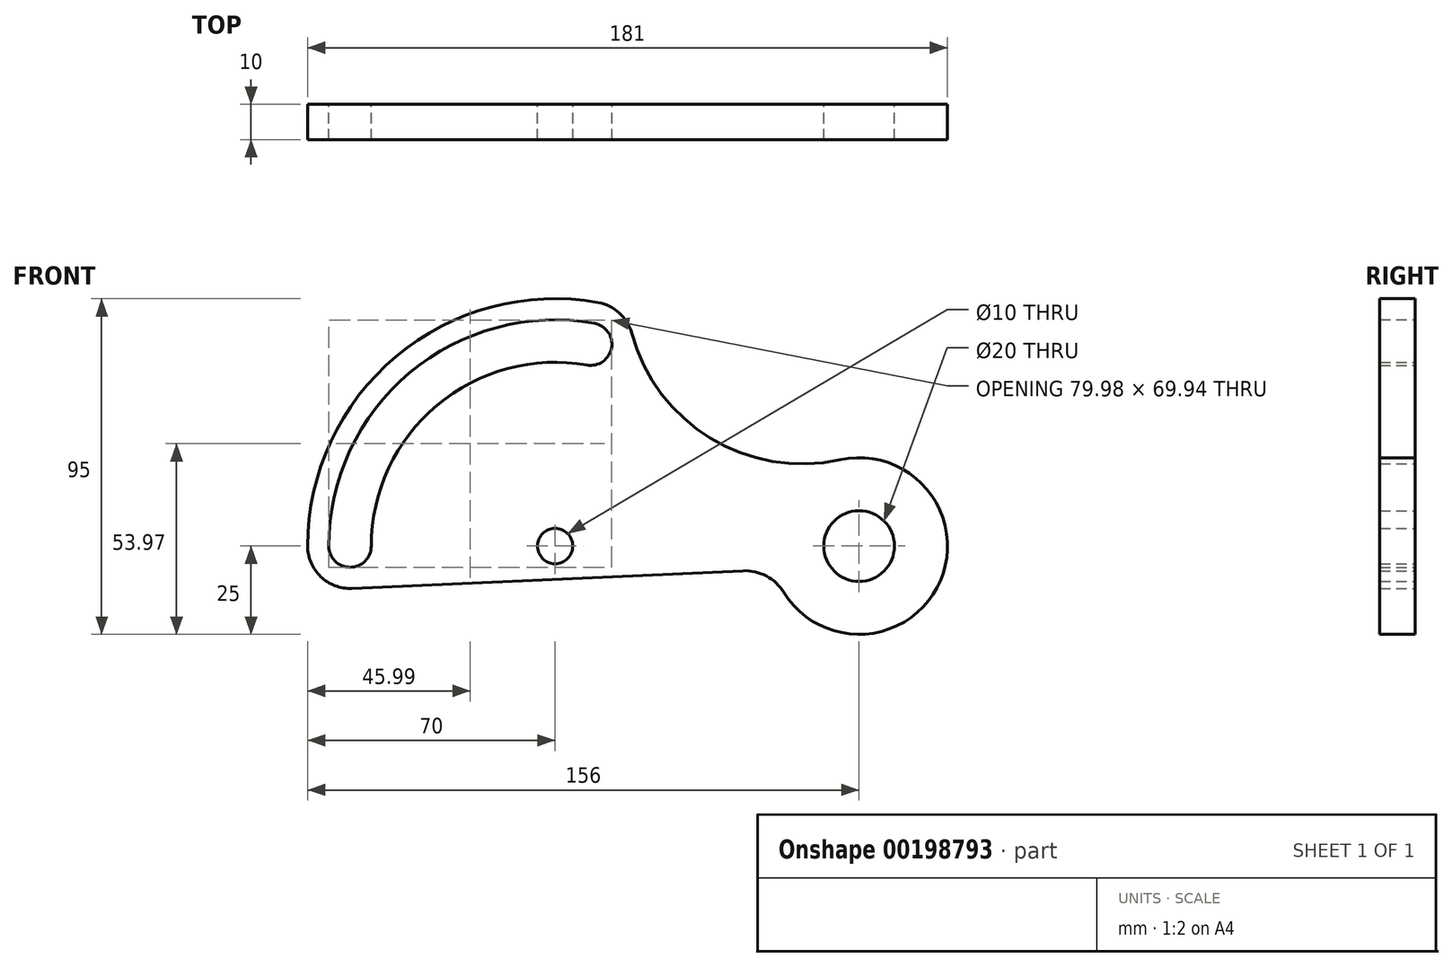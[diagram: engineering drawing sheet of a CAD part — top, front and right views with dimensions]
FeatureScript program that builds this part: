
annotation { "Feature Type Name" : "Feature", "Feature Type Description" : "" }
export const myFeature = defineFeature(function(context is Context, id is Id, definition is map)
    precondition{}
    {
        {
            var Q0;
            Q0=qCreatedBy(makeId("Front.planeOp"),FACE);
            var sketch = newSketch(context, id + "F0", { "sketchPlane" : qUnion([Q0])});
            skCircle(sketch, "E0", {"center": v(0, 0) * mm, "radius": 5 * mm});
            skLineSegment(sketch, "E1", {"start": v(0, 0) * mm, "end": v(0, 3.4) * mm});
            skLineSegment(sketch, "E2", {"start": v(0, 0) * mm, "end": v(10.07, 57.12) * mm, "construction": true});
            skArc(sketch, "E3", {"start": v(-58, 0) * mm, "mid": v(-37.28, 44.43) * mm, "end": v(10.07, 57.12) * mm, "construction": true});
            skArc(sketch, "E4", {"start": v(11.11, 63.03) * mm, "mid": v(-41.14, 49.03) * mm, "end": v(-64, 0) * mm});
            skArc(sketch, "E5", {"start": v(9.03, 51.21) * mm, "mid": v(-33.42, 39.83) * mm, "end": v(-52, 0) * mm});
            skArc(sketch, "E6", {"start": v(9.03, 51.21) * mm, "mid": v(15.98, 56.08) * mm, "end": v(11.11, 63.03) * mm});
            skArc(sketch, "E7", {"start": v(-64, 0) * mm, "mid": v(-58, -6) * mm, "end": v(-52, 0) * mm});
            skArc(sketch, "E8", {"start": v(12.16, 68.94) * mm, "mid": v(-45, 53.62) * mm, "end": v(-70, 0) * mm});
            skArc(sketch, "E9", {"start": v(21.66, 60.24) * mm, "mid": v(18.17, 65.97) * mm, "end": v(12.16, 68.94) * mm});
            skArc(sketch, "E10", {"start": v(-70, 0) * mm, "mid": v(-66.3, -8.67) * mm, "end": v(-57.46, -11.99) * mm});
            skCircle(sketch, "E11", {"center": v(86, 0) * mm, "radius": 10 * mm});
            skArc(sketch, "E12", {"start": v(80.64, 24.42) * mm, "mid": v(109.02, -9.74) * mm, "end": v(64.74, -13.16) * mm});
            skArc(sketch, "E13", {"start": v(21.66, 60.24) * mm, "mid": v(43.98, 30.52) * mm, "end": v(80.64, 24.42) * mm});
            skLineSegment(sketch, "E14", {"start": v(-57.46, -11.99) * mm, "end": v(53.1, -7.01) * mm});
            skPoint(sketch, "E15.visualSharp", {"position": v(61.9, -6.62) * mm});
            skArc(sketch, "E15.filletArc", {"start": v(64.74, -13.16) * mm, "mid": v(59.76, -8.5) * mm, "end": v(53.1, -7.01) * mm});
            skSolve(sketch);
        }
        {
            var Q0;
            Q0=makeQuery(id+"F0.imprint","IMPRINT",FACE,{"disambiguationData":[TD([[makeQuery(id+"F0.imprint","IMPRINT",EDGE,{"derivedFrom":sQuery(id+"F0.wireOp",EDGE,"E0")}),-1.0]])]});
            extrude(context, id + "F1", {"entities" : qUnion([Q0]), "depth" : 10 * mm});
        }
    });
